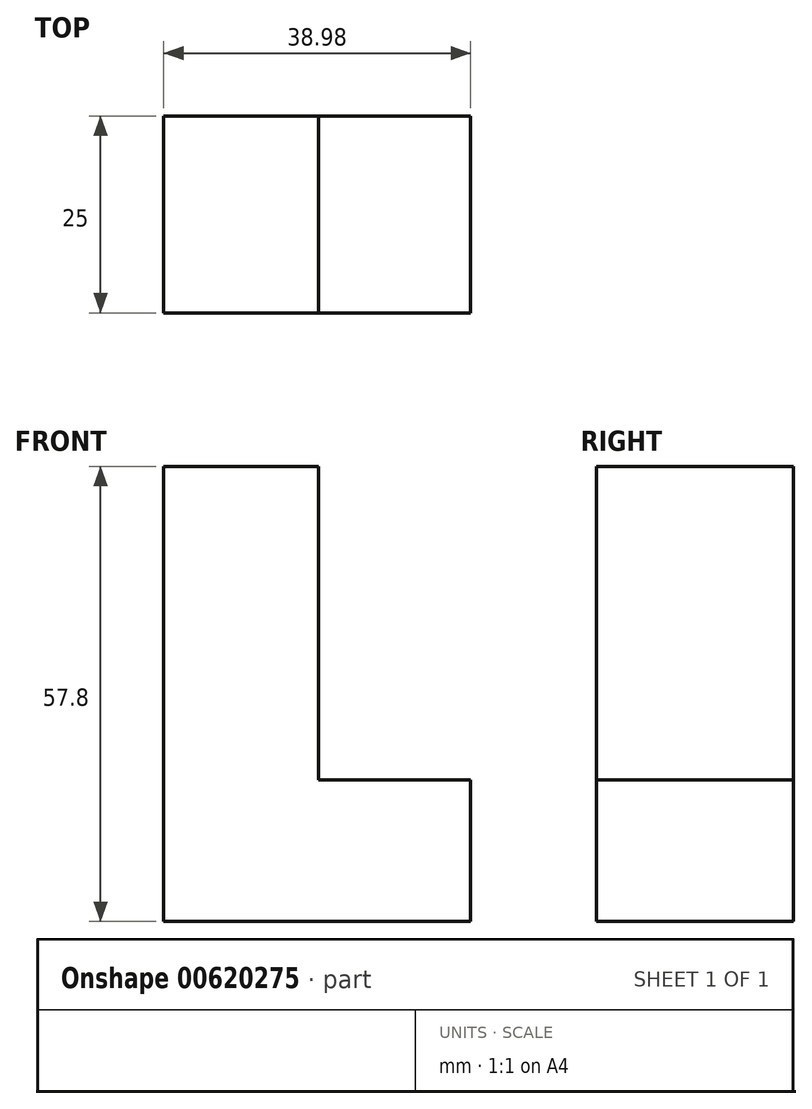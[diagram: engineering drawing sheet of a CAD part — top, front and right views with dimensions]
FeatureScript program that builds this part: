
annotation { "Feature Type Name" : "Feature", "Feature Type Description" : "" }
export const myFeature = defineFeature(function(context is Context, id is Id, definition is map)
    precondition{}
    {
        {
            var Q0;
            Q0=qCreatedBy(makeId("Front.planeOp"),FACE);
            var sketch = newSketch(context, id + "F0", { "sketchPlane" : qUnion([Q0])});
            skLineSegment(sketch, "E0", {"start": v(-31.2, 40.94) * mm, "end": v(-11.55, 40.94) * mm});
            skLineSegment(sketch, "E1", {"start": v(-11.55, 40.94) * mm, "end": v(-11.55, 1.14) * mm});
            skLineSegment(sketch, "E2", {"start": v(-11.55, 1.14) * mm, "end": v(7.8, 1.14) * mm});
            skLineSegment(sketch, "E3", {"start": v(7.8, 1.14) * mm, "end": v(7.8, -16.86) * mm});
            skLineSegment(sketch, "E4", {"start": v(7.8, -16.86) * mm, "end": v(-31.2, -16.86) * mm});
            skLineSegment(sketch, "E5", {"start": v(-31.2, -16.86) * mm, "end": v(-31.2, 40.94) * mm});
            skSolve(sketch);
        }
        {
            var Q0;
            Q0=makeQuery(id+"F0.imprint","IMPRINT",FACE,{"disambiguationData":[TD([[makeQuery(id+"F0.imprint","IMPRINT",EDGE,{"derivedFrom":sQuery(id+"F0.wireOp",EDGE,"E0")}),-1.0]])]});
            extrude(context, id + "F1", {"entities" : qUnion([Q0]), "depth" : 25 * mm, "offsetDistance" : 25 * mm});
        }
    });
